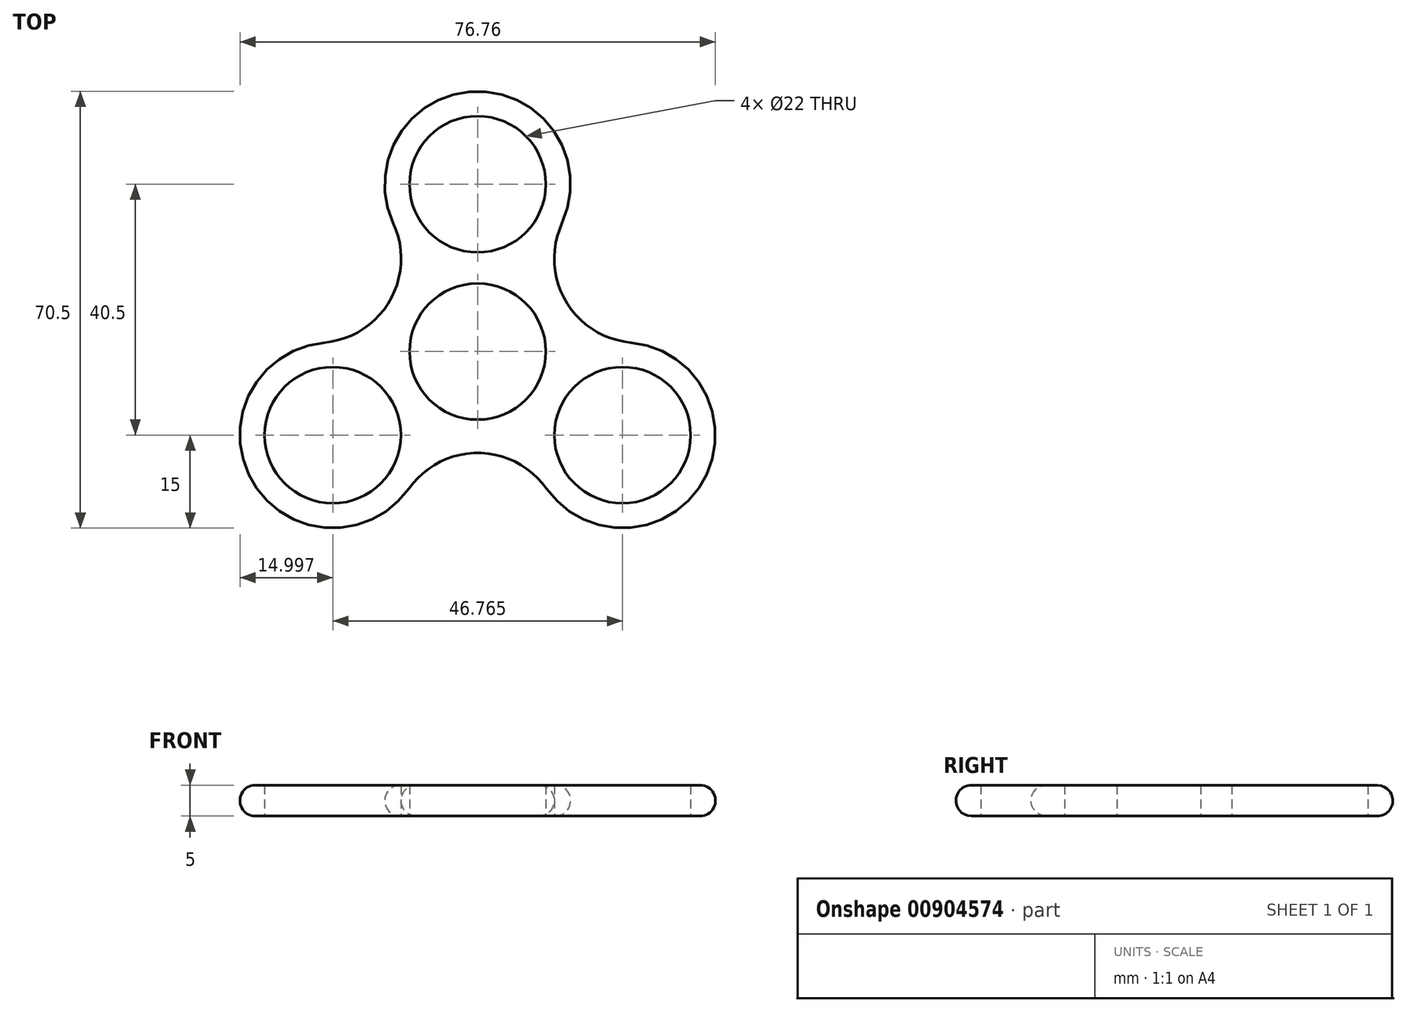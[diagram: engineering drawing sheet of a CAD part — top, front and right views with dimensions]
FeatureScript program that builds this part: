
annotation { "Feature Type Name" : "Feature", "Feature Type Description" : "" }
export const myFeature = defineFeature(function(context is Context, id is Id, definition is map)
    precondition{}
    {
        {
            var Q0;
            Q0=qCreatedBy(makeId("Top.planeOp"),FACE);
            var sketch = newSketch(context, id + "F0", { "sketchPlane" : qUnion([Q0])});
            skCircle(sketch, "E0", {"center": v(0, 27) * mm, "radius": 11 * mm});
            skArc(sketch, "E1", {"start": v(13.62, 20.71) * mm, "mid": v(0, 42) * mm, "end": v(-13.62, 20.71) * mm});
            skCircle(sketch, "E2.1.0", {"center": v(-23.38, -13.5) * mm, "radius": 11 * mm});
            skArc(sketch, "E2.1.1", {"start": v(-24.74, 1.44) * mm, "mid": v(-36.37, -21) * mm, "end": v(-11.13, -22.15) * mm});
            skCircle(sketch, "E2.2.0", {"center": v(23.38, -13.5) * mm, "radius": 11 * mm});
            skArc(sketch, "E2.2.1", {"start": v(11.13, -22.15) * mm, "mid": v(36.37, -21) * mm, "end": v(24.74, 1.44) * mm});
            skPoint(sketch, "E2.center", {"position": v(0, 0) * mm});
            skArc(sketch, "E3", {"start": v(11.13, -22.15) * mm, "mid": v(0, -16.38) * mm, "end": v(-11.13, -22.15) * mm});
            skCircle(sketch, "E4", {"center": v(0, 0) * mm, "radius": 11 * mm});
            skArc(sketch, "E5.1.0", {"start": v(13.62, 20.71) * mm, "mid": v(14.19, 8.2) * mm, "end": v(24.74, 1.44) * mm});
            skArc(sketch, "E5.2.0", {"start": v(-24.74, 1.44) * mm, "mid": v(-14.19, 8.2) * mm, "end": v(-13.62, 20.71) * mm});
            skSolve(sketch);
        }
        {
            var Q0;
            Q0 = qSketchRegion(id + "F0", true);
            extrude(context, id + "F1", {"entities" : qUnion([Q0]), "endBound" : BoundingType.SYMMETRIC, "depth" : 5 * mm, "offsetDistance" : 25 * mm});
        }
        {
            var Q0;
            Q0=makeQuery(id+"F1.opExtrude","SWEPT_FACE",FACE,{"disambiguationData":[OSD([sQuery(id+"F0.wireOp",EDGE,"E2.1.1")])]});
            var Q1;
            Q1=makeQuery(id+"F1.opExtrude","SWEPT_FACE",FACE,{"disambiguationData":[OSD([sQuery(id+"F0.wireOp",EDGE,"E1")])]});
            var Q2;
            Q2=makeQuery(id+"F1.opExtrude","SWEPT_FACE",FACE,{"disambiguationData":[OSD([sQuery(id+"F0.wireOp",EDGE,"E5.2.0")])]});
            var Q3;
            Q3=makeQuery(id+"F1.opExtrude","SWEPT_FACE",FACE,{"disambiguationData":[OSD([sQuery(id+"F0.wireOp",EDGE,"E5.1.0")])]});
            var Q4;
            Q4=makeQuery(id+"F1.opExtrude","SWEPT_FACE",FACE,{"disambiguationData":[OSD([sQuery(id+"F0.wireOp",EDGE,"E3")])]});
            var Q5;
            Q5=makeQuery(id+"F1.opExtrude","SWEPT_FACE",FACE,{"disambiguationData":[OSD([sQuery(id+"F0.wireOp",EDGE,"E2.2.1")])]});
            fillet(context, id + "F2", {"entities" : qUnion([Q0, Q1, Q2, Q3, Q4, Q5]), "radius" : 2.5 * mm, "tangentPropagation" : true, "allowEdgeOverflow" : false});
        }
    });
